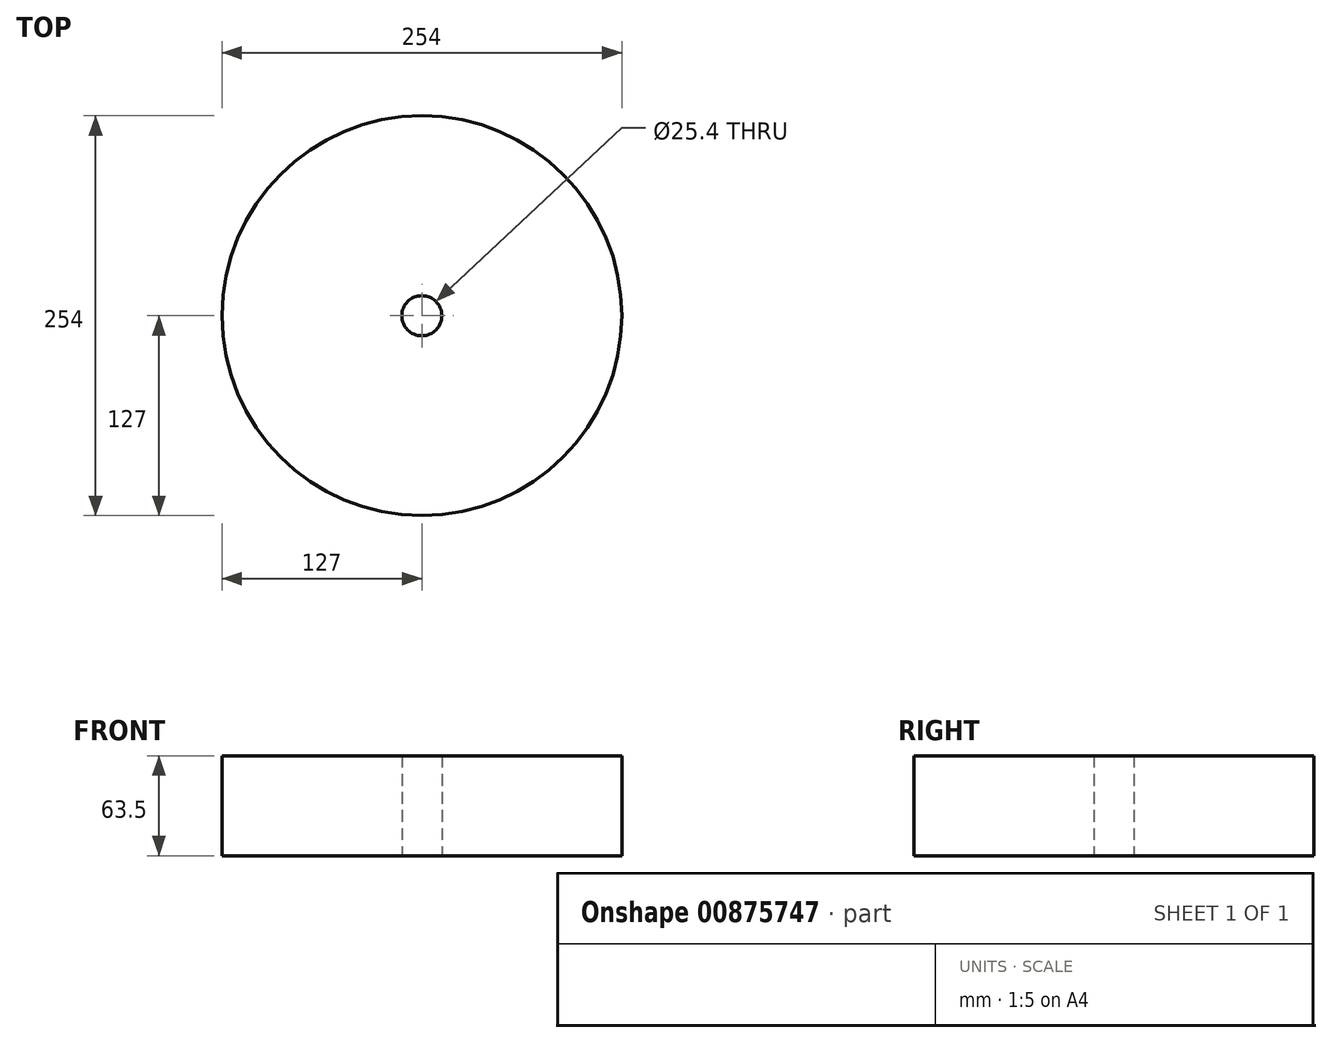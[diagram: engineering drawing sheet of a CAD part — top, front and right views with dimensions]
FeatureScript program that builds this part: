
annotation { "Feature Type Name" : "Feature", "Feature Type Description" : "" }
export const myFeature = defineFeature(function(context is Context, id is Id, definition is map)
    precondition{}
    {
        {
            var Q0;
            Q0=qCreatedBy(makeId("Top.planeOp"),FACE);
            var sketch = newSketch(context, id + "F0", { "sketchPlane" : qUnion([Q0])});
            skCircle(sketch, "E0", {"center": v(0, 0) * mm, "radius": 127 * mm});
            skCircle(sketch, "E1", {"center": v(0, 0) * mm, "radius": 12.7 * mm});
            skSolve(sketch);
        }
        {
            var Q0;
            Q0=makeQuery(id+"F0.imprint","IMPRINT",FACE,{"disambiguationData":[TD([[makeQuery(id+"F0.imprint","IMPRINT",EDGE,{"derivedFrom":sQuery(id+"F0.wireOp",EDGE,"E0")}),1.0]])]});
            extrude(context, id + "F1", {"entities" : qUnion([Q0]), "depth" : 63.5 * mm, "offsetDistance" : 25.4 * mm});
        }
    });
